AUTODESK INVENTOR PART (.ipt)
format: ipt  version: 2014 (Build 180170000, 170)  size: 158,208 bytes
history: native  units: in
note: dims shown in document units (in); Inventor stores cm internally (conversion verified against a paired STEP export)
features: plane x3, extrude x2, sketch x2, fillet x1, pattern_circular x1, reference x1
ambient origin geometry x8: Origin, YZ Plane, XZ Plane, XY Plane, X Axis, Y Axis, Z Axis, Center Point
bodies: Solid1 (feature_tree), Solid2 (feature_tree)
feature tree (10):
  plane  "Work Plane1"
  plane  "Work Plane2"
  extrude  "Extrusion1"  Depth=0.2362in TaperAngle=0.0deg
  fillet  "Fillet1"  Radius=0.0394in
  plane  "Work Plane3"
  extrude  "Extrusion2"  Depth=0.0787in
  pattern_circular  "Circular Pattern1"  [2 undecoded]
  sketch  "Sketch1"  dims[d0=0.2559in d1=0.2362in d2=0.0in d3=0.0394in]
  reference  "Reference1"
  sketch  "Sketch2"  dims[d4=-0.1181in d5=0.0787in d6=0.1969in d7=0.0197in d8=0.0in d9=4.7244in d10=360.0deg]
note: 2 required parameter values undecoded (feature->parameter linkage not recoverable at this tier; creation-order binding heuristic only, values carry confidence <= 0.55)
